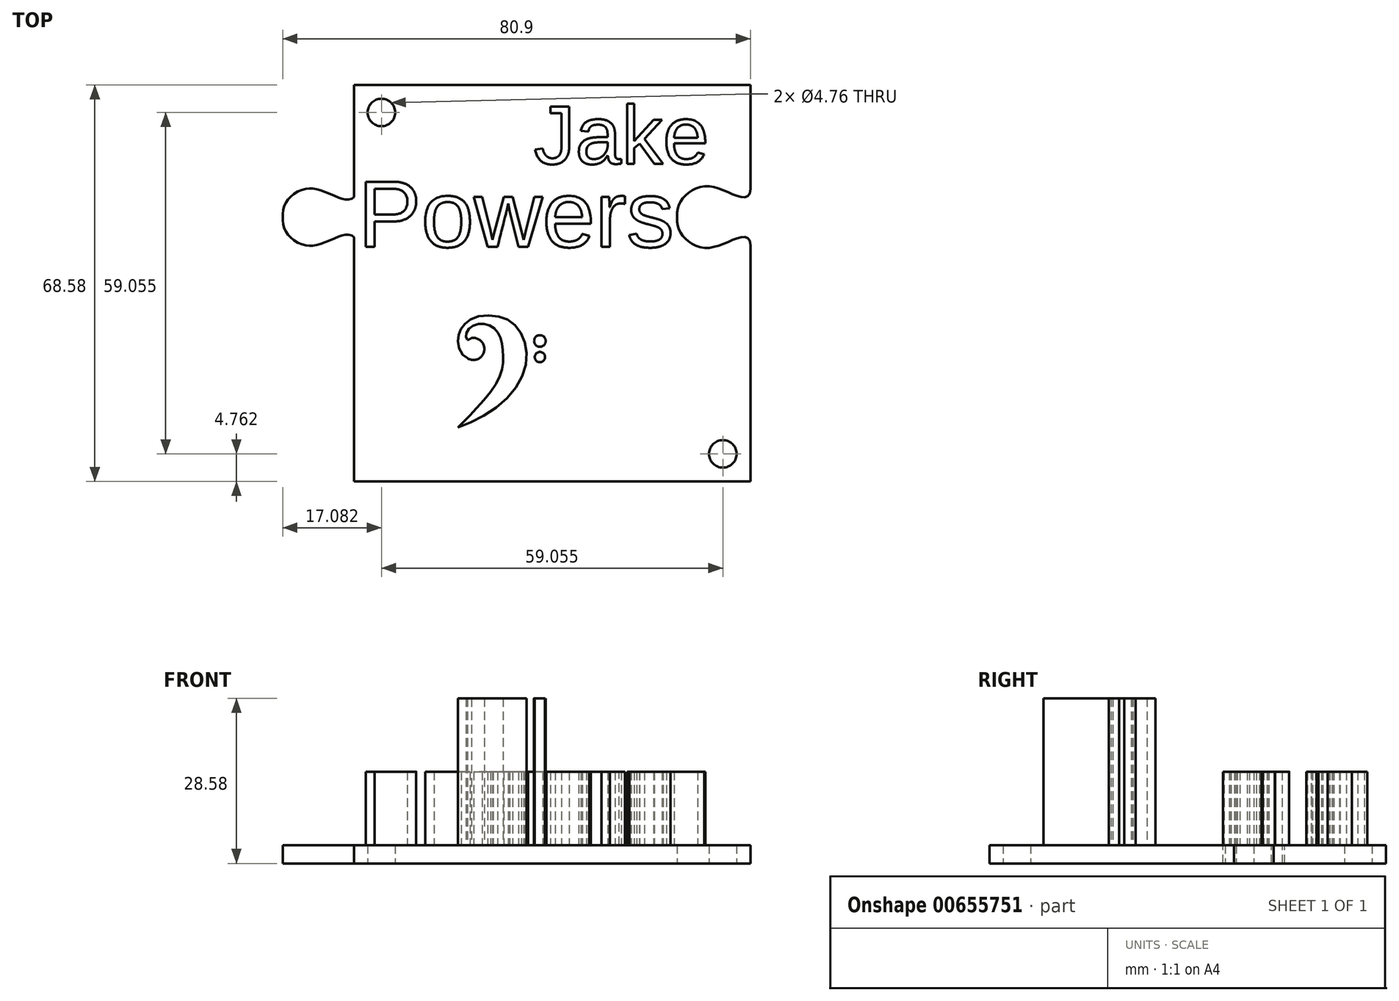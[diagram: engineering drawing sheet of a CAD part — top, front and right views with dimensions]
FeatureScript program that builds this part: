
annotation { "Feature Type Name" : "Feature", "Feature Type Description" : "" }
export const myFeature = defineFeature(function(context is Context, id is Id, definition is map)
    precondition{}
    {
        {
            var Q0;
            Q0=qCreatedBy(makeId("Top.planeOp"),FACE);
            var sketch = newSketch(context, id + "F0", { "sketchPlane" : qUnion([Q0])});
            skLineSegment(sketch, "E0.bottom", {"start": v(34.3, 34.3) * mm, "end": v(-34.3, 34.3) * mm});
            skLineSegment(sketch, "E0.top", {"start": v(34.3, -34.3) * mm, "end": v(-34.3, -34.3) * mm});
            skLineSegment(sketch, "E0.left", {"start": v(34.3, 34.3) * mm, "end": v(34.3, -34.3) * mm});
            skLineSegment(sketch, "E0.right", {"start": v(-34.3, 34.3) * mm, "end": v(-34.3, -34.3) * mm});
            skPoint(sketch, "E0.middle", {"position": v(0, 0) * mm});
            skCircle(sketch, "E1", {"center": v(-29.53, 29.53) * mm, "radius": 2.38 * mm});
            skCircle(sketch, "E2.MirrorC", {"center": v(29.53, -29.53) * mm, "radius": 2.38 * mm});
            skSolve(sketch);
        }
        {
            var Q0;
            Q0=qSketchRegion(id+"F0",true);
            extrude(context, id + "F1", {"entities" : qUnion([Q0]), "depth" : 3.17 * mm});
        }
        {
            var Q0;
            Q0=qCreatedBy(makeId("Top.planeOp"),FACE);
            var sketch = newSketch(context, id + "F2", { "sketchPlane" : qUnion([Q0])});
            skPoint(sketch, "E3", {"position": v(-34.3, 16.33) * mm});
            skPoint(sketch, "E4", {"position": v(-36.2, 14.99) * mm});
            skPoint(sketch, "E5", {"position": v(-41.66, 16.76) * mm});
            skPoint(sketch, "E6", {"position": v(-45.72, 14.99) * mm});
            skPoint(sketch, "E7", {"position": v(-47, 11.43) * mm});
            skFitSpline(sketch, "E8", {"points": [v(-34.3, 16.33) * mm, v(-36.2, 14.99) * mm, v(-41.66, 16.76) * mm, v(-45.72, 14.99) * mm, v(-47, 11.43) * mm], "startDerivative": vector(0, -24.54) * mm, "endDerivative": vector(0, -20.15) * mm});
            skLineSegment(sketch, "E9", {"start": v(-47, 11.43) * mm, "end": v(-29.95, 11.43) * mm, "construction": true});
            skFitSpline(sketch, "E10.MirrorCS", {"points": [v(-34.3, 6.53) * mm, v(-36.2, 7.87) * mm, v(-41.66, 6.1) * mm, v(-45.72, 7.87) * mm, v(-47, 11.43) * mm], "startDerivative": vector(0, 24.54) * mm, "endDerivative": vector(0, 20.15) * mm});
            skLineSegment(sketch, "E11", {"start": v(-34.3, 16.33) * mm, "end": v(-34.3, 6.53) * mm, "construction": true});
            skFitSpline(sketch, "E12.MirrorCS", {"points": [v(-34.3, 16.33) * mm, v(-32.39, 14.99) * mm, v(-26.92, 16.76) * mm, v(-22.86, 14.99) * mm, v(-21.59, 11.43) * mm], "startDerivative": vector(0, -24.54) * mm, "endDerivative": vector(0, -20.15) * mm});
            skFitSpline(sketch, "E13.MirrorCS", {"points": [v(-34.3, 6.53) * mm, v(-32.39, 7.87) * mm, v(-26.92, 6.1) * mm, v(-22.86, 7.87) * mm, v(-21.59, 11.43) * mm], "startDerivative": vector(0, 24.54) * mm, "endDerivative": vector(0, 20.15) * mm});
            skFitSpline(sketch, "E14.0", {"points": [v(-33.9, 6.53) * mm, v(-33.9, 6.8) * mm, v(-33.96, 7.3) * mm, v(-34.16, 7.77) * mm, v(-34.42, 8.07) * mm, v(-34.73, 8.28) * mm, v(-35.16, 8.4) * mm, v(-35.7, 8.38) * mm, v(-36.22, 8.27) * mm, v(-36.76, 8.1) * mm, v(-37.5, 7.83) * mm, v(-38.44, 7.42) * mm, v(-39.6, 6.94) * mm, v(-40.54, 6.64) * mm, v(-41.28, 6.5) * mm, v(-41.8, 6.46) * mm, v(-42.32, 6.5) * mm, v(-43, 6.62) * mm, v(-43.8, 6.91) * mm, v(-44.68, 7.44) * mm, v(-45.29, 7.96) * mm, v(-45.69, 8.4) * mm, v(-46.02, 8.85) * mm, v(-46.33, 9.45) * mm, v(-46.56, 10.3) * mm, v(-46.6, 11.03) * mm, v(-46.6, 11.43) * mm]});
            skFitSpline(sketch, "E14.1", {"points": [v(-33.9, 16.33) * mm, v(-33.9, 16.05) * mm, v(-33.96, 15.56) * mm, v(-34.16, 15.09) * mm, v(-34.42, 14.8) * mm, v(-34.73, 14.58) * mm, v(-35.16, 14.46) * mm, v(-35.7, 14.48) * mm, v(-36.22, 14.6) * mm, v(-36.76, 14.76) * mm, v(-37.5, 15.03) * mm, v(-38.44, 15.44) * mm, v(-39.6, 15.92) * mm, v(-40.54, 16.22) * mm, v(-41.28, 16.36) * mm, v(-41.8, 16.4) * mm, v(-42.32, 16.37) * mm, v(-43, 16.24) * mm, v(-43.8, 15.95) * mm, v(-44.68, 15.42) * mm, v(-45.29, 14.9) * mm, v(-45.69, 14.46) * mm, v(-46.02, 14.01) * mm, v(-46.33, 13.41) * mm, v(-46.56, 12.55) * mm, v(-46.6, 11.83) * mm, v(-46.6, 11.43) * mm]});
            skLineSegment(sketch, "E15", {"start": v(-34.3, 16.33) * mm, "end": v(-34.3, 6.53) * mm});
            skLineSegment(sketch, "E16", {"start": v(-34.3, 7.92) * mm, "end": v(-34.3, 14.94) * mm});
            skFitSpline(sketch, "E17.MirrorCS", {"points": [v(34.3, 16.33) * mm, v(32.39, 14.99) * mm, v(26.92, 16.76) * mm, v(22.86, 14.99) * mm, v(21.59, 11.43) * mm], "startDerivative": vector(0, -24.54) * mm, "endDerivative": vector(0, -20.15) * mm});
            skFitSpline(sketch, "E18.MirrorCS", {"points": [v(34.3, 6.53) * mm, v(32.39, 7.87) * mm, v(26.92, 6.1) * mm, v(22.86, 7.87) * mm, v(21.59, 11.43) * mm], "startDerivative": vector(0, 24.54) * mm, "endDerivative": vector(0, 20.15) * mm});
            skLineSegment(sketch, "E19", {"start": v(34.3, 16.33) * mm, "end": v(39.12, 16.33) * mm});
            skLineSegment(sketch, "E20", {"start": v(39.12, 16.33) * mm, "end": v(39.12, 6.53) * mm});
            skLineSegment(sketch, "E21", {"start": v(39.12, 6.53) * mm, "end": v(34.3, 6.53) * mm});
            skSolve(sketch);
        }
        {
            var Q0;
            Q0=makeQuery(id+"F2.imprint","IMPRINT",FACE,{"disambiguationData":[TD([[makeQuery(id+"F2.imprint","IMPRINT",EDGE,{"derivedFrom":sQuery(id+"F2.wireOp",EDGE,"E14.0")}),-1.0]])]});
            var Q1;
            Q1=makeQuery(id+"F1.opExtrude","CAP_FACE",FACE,{"disambiguationData":[OSD([sQuery(id+"F0.wireOp",EDGE,"E0.bottom"),sQuery(id+"F0.wireOp",EDGE,"E0.top"),sQuery(id+"F0.wireOp",EDGE,"E0.left"),sQuery(id+"F0.wireOp",EDGE,"E0.right"),sQuery(id+"F0.wireOp",EDGE,"E1"),sQuery(id+"F0.wireOp",EDGE,"e1648c08-8adf-473f-9b64-c467cf328ef90.MirrorC"),sQuery(id+"F0.wireOp",EDGE,"1cdcda55-2210-49d8-b5f0-9198a802923b0.MirrorC"),sQuery(id+"F0.wireOp",EDGE,"E2.MirrorC")])],"isStart":false});
            extrude(context, id + "F3", {"entities" : qUnion([Q0]), "operationType" : NewBodyOperationType.ADD, "endBound" : BoundingType.UP_TO_SURFACE, "endBoundEntityFace" : qUnion([Q1]), "depth" : 25.4 * mm});
        }
        {
            var Q0;
            Q0=qCreatedBy(makeId("Right.planeOp"),FACE);
            var sketch = newSketch(context, id + "F4", { "sketchPlane" : qUnion([Q0])});
            skLineSegment(sketch, "E22", {"start": v(0, -65.87) * mm, "end": v(0, 47.63) * mm});
            skSolve(sketch);
        }
        {
            var Q0;
            Q0=makeQuery(id+"F2.imprint","IMPRINT",FACE,{"disambiguationData":[TD([[makeQuery(id+"F2.imprint","IMPRINT",EDGE,{"derivedFrom":sQuery(id+"F2.wireOp",EDGE,"E17.MirrorCS")}),1.0]])]});
            extrude(context, id + "F5", {"entities" : qUnion([Q0]), "operationType" : NewBodyOperationType.REMOVE, "endBound" : BoundingType.THROUGH_ALL, "depth" : 25.4 * mm});
        }
        {
            var Q0;
            {var subQ0=sQuery(id+"F0.wireOp",EDGE,"E2.MirrorC");var subQ1=sQuery(id+"F0.wireOp",EDGE,"E1");var subQ2=sQuery(id+"F0.wireOp",EDGE,"E0.right");var subQ3=sQuery(id+"F0.wireOp",EDGE,"E0.left");var subQ4=sQuery(id+"F0.wireOp",EDGE,"E0.top");var subQ5=sQuery(id+"F0.wireOp",EDGE,"E0.bottom");Q0=makeQuery(id+"FDfX84p6046V9zH_1.3.F3.boolean.opBoolean","MERGE",FACE,{"derivedFrom":[makeQuery(id+"FDfX84p6046V9zH_1.2.F3.boolean.opBoolean","MERGE",FACE,{"derivedFrom":[makeQuery(id+"FDfX84p6046V9zH_1.1.F3.boolean.opBoolean","MERGE",FACE,{"derivedFrom":[makeQuery(id+"F3.boolean.opBoolean","MERGE",FACE,{"derivedFrom":[makeQuery(id+"F1.opExtrude","CAP_FACE",FACE,{"disambiguationData":[OSD([subQ5,subQ4,subQ3,subQ2,subQ1,subQ0])],"isStart":false}),makeQuery(id+"F3.opExtrude","CAP_FACE",FACE,{"disambiguationData":[OSD([subQ5,subQ4,subQ3,subQ2,subQ1,subQ0])],"isStart":false})]}),makeQuery(id+"FDfX84p6046V9zH_1.1.F3.opExtrude","CAP_FACE",FACE,{"disambiguationData":[OSD([subQ5,subQ4,subQ3,subQ2,subQ1,subQ0])],"isStart":false})]}),makeQuery(id+"FDfX84p6046V9zH_1.2.F3.opExtrude","CAP_FACE",FACE,{"disambiguationData":[OSD([subQ5,subQ4,subQ3,subQ2,subQ1,subQ0])],"isStart":false})]}),makeQuery(id+"FDfX84p6046V9zH_1.3.F3.opExtrude","CAP_FACE",FACE,{"disambiguationData":[OSD([subQ5,subQ4,subQ3,subQ2,subQ1,subQ0])],"isStart":false})]});}
            var sketch = newSketch(context, id + "F6", { "sketchPlane" : qUnion([Q0])});
            skText(sketch, "E23", { "text": "Jake", "fontName": "Arimo-Regular.ttf"});
            skText(sketch, "E24", { "text": "Powers", "fontName": "Arimo-Regular.ttf"});
            const initialGuessF6  = {"E23": [-0.00315, 0.02066, 1, 0, 0.01032], "E24": [-0.03357, 0.00628, 1, 0, 0.0118]};
            skSetInitialGuess(sketch, initialGuessF6);
            skSolve(sketch);
        }
        {
            var Q0;
            Q0 = qSketchRegion(id + "F6", true);
            extrude(context, id + "F7", {"entities" : qUnion([Q0]), "operationType" : NewBodyOperationType.ADD, "depth" : 12.7 * mm, "offsetDistance" : 25.4 * mm});
        }
        {
            var Q0;
            {var subQ4=sQuery(id+"F0.wireOp",EDGE,"E1");var subQ5=sQuery(id+"F0.wireOp",EDGE,"E0.right");var subQ6=sQuery(id+"F0.wireOp",EDGE,"E0.bottom");var subQ7=sQuery(id+"F0.wireOp",EDGE,"E0.left");var subQ8=sQuery(id+"F0.wireOp",EDGE,"E0.top");var subQ9=sQuery(id+"F0.wireOp",EDGE,"E2.MirrorC");Q0=makeQuery(id+"F7.boolean.opBoolean","SPLIT",FACE,{"disambiguationData":[TD([makeQuery(id+"F1.opExtrude","SWEPT_FACE",FACE,{"disambiguationData":[OSD([subQ6])]})])],"derivedFrom":makeQuery(id+"FDfX84p6046V9zH_1.3.F3.boolean.opBoolean","MERGE",FACE,{"derivedFrom":[makeQuery(id+"FDfX84p6046V9zH_1.2.F3.boolean.opBoolean","MERGE",FACE,{"derivedFrom":[makeQuery(id+"FDfX84p6046V9zH_1.1.F3.boolean.opBoolean","MERGE",FACE,{"derivedFrom":[makeQuery(id+"F3.boolean.opBoolean","MERGE",FACE,{"derivedFrom":[makeQuery(id+"F1.opExtrude","CAP_FACE",FACE,{"disambiguationData":[OSD([subQ6,subQ8,subQ7,subQ5,subQ4,subQ9])],"isStart":false}),makeQuery(id+"F3.opExtrude","CAP_FACE",FACE,{"disambiguationData":[OSD([subQ6,subQ8,subQ7,subQ5,subQ4,subQ9])],"isStart":false})]}),makeQuery(id+"FDfX84p6046V9zH_1.1.F3.opExtrude","CAP_FACE",FACE,{"disambiguationData":[OSD([subQ6,subQ8,subQ7,subQ5,subQ4,subQ9])],"isStart":false})]}),makeQuery(id+"FDfX84p6046V9zH_1.2.F3.opExtrude","CAP_FACE",FACE,{"disambiguationData":[OSD([subQ6,subQ8,subQ7,subQ5,subQ4,subQ9])],"isStart":false})]}),makeQuery(id+"FDfX84p6046V9zH_1.3.F3.opExtrude","CAP_FACE",FACE,{"disambiguationData":[OSD([subQ6,subQ8,subQ7,subQ5,subQ4,subQ9])],"isStart":false})]})});}
            var sketch = newSketch(context, id + "F8", { "sketchPlane" : qUnion([Q0])});
            skCircle(sketch, "E25", {"center": v(-13.63, -11.37) * mm, "radius": 1.9 * mm});
            skFitSpline(sketch, "E26", {"points": [v(-13.92, -9.49) * mm, v(-14.67, -9.78) * mm, v(-14.78, -8.46) * mm, v(-12.38, -7.04) * mm, v(-9.51, -8.4) * mm, v(-8.5, -12.2) * mm, v(-9.63, -17.27) * mm, v(-16.27, -24.96) * mm], "startDerivative": vector(-12.06, -5.4) * mm, "endDerivative": vector(-17.82, -18.72) * mm});
            skFitSpline(sketch, "E27", {"points": [v(-14.65, -12.98) * mm, v(-16, -11.43) * mm, v(-16.23, -9.25) * mm, v(-15.54, -7.59) * mm, v(-13.63, -6.02) * mm, v(-9.08, -5.79) * mm, v(-5.8, -8.02) * mm, v(-4.45, -13.15) * mm, v(-7.82, -19.92) * mm, v(-16.27, -24.96) * mm], "startDerivative": vector(-19.98, 2.82) * mm, "endDerivative": vector(-48.27, -17.12) * mm});
            skCircle(sketch, "E28", {"center": v(-2.11, -10) * mm, "radius": 1 * mm});
            skCircle(sketch, "E29", {"center": v(-2.11, -12.79) * mm, "radius": 0.89 * mm});
            skSolve(sketch);
        }
        {
            var Q0;
            {var subQ0=sQuery(id+"F8.wireOp",EDGE,"E25");var subQ1=makeQuery(id+"F8.imprint","INTERSECT",VERTEX,{"derivedFrom":[subQ0,sQuery(id+"F8.wireOp",EDGE,"E27")]});Q0=makeQuery(id+"F8.imprint","IMPRINT",FACE,{"disambiguationData":[TD([[makeQuery(id+"F8.imprint","IMPRINT",EDGE,{"disambiguationData":[TD([[subQ1,1.0]])],"derivedFrom":subQ0}),1.0]])]});}
            var Q1;
            {var subQ0=sQuery(id+"F8.wireOp",EDGE,"E27");Q1=makeQuery(id+"F8.imprint","IMPRINT",FACE,{"disambiguationData":[TD([[makeQuery(id+"F8.imprint","IMPRINT",EDGE,{"derivedFrom":subQ0}),-1.0]])]});}
            extrude(context, id + "F9", {"entities" : qUnion([Q0, Q1]), "operationType" : NewBodyOperationType.ADD, "depth" : 25.4 * mm, "offsetDistance" : 25.4 * mm});
        }
        {
            var Q0;
            Q0=makeQuery(id+"F8.imprint","IMPRINT",FACE,{"disambiguationData":[TD([[makeQuery(id+"F8.imprint","IMPRINT",EDGE,{"derivedFrom":sQuery(id+"F8.wireOp",EDGE,"E28")}),1.0]])]});
            extrude(context, id + "F10", {"entities" : qUnion([Q0]), "operationType" : NewBodyOperationType.ADD, "depth" : 25.4 * mm, "offsetDistance" : 25.4 * mm});
        }
        {
            var Q0;
            Q0=makeQuery(id+"F8.imprint","IMPRINT",FACE,{"disambiguationData":[TD([[makeQuery(id+"F8.imprint","IMPRINT",EDGE,{"derivedFrom":sQuery(id+"F8.wireOp",EDGE,"E29")}),1.0]])]});
            extrude(context, id + "F11", {"entities" : qUnion([Q0]), "operationType" : NewBodyOperationType.ADD, "depth" : 25.4 * mm, "offsetDistance" : 25.4 * mm});
        }
    });
